# Revit family: DC_Holyoake_MEQ_FSD-200_12
name_source: partatom
category: Air Terminals
revit_build: Autodesk Revit MEP 2013 (Build: 20120221_2030(x64)
units: mm (PartAtom-declared; Revit-internal decimal feet)

## types (1)
- FSD 200
    Connector Rad = 65 mm  [stored 0.213255 ft]
    Description = Floor Swirl Diffusers shall be Holyoake Model FSD-200 Floor Swirl Diffusers. The diffusers shall be constructed entirely of high impact polycarbonate which complies with UL Standard 94-5V for flammability. The core design shall produce a high velocity helical swirl discharge air pattern. The diffusers shall incorporate a removable dust/dirt collection basket. An air flow regulator damper, adjustable without removing the diffuser core, shall be provided with visual open/closed indication and include an adjustable minimum volume stop. Finish on visible surfaces shall be Grey or Black (selected Finishes available).
    Finish = Holyoake Black
    Holyoake Product Range = Holyoake FSD Floor Swirl Diffuser
    Manufacturer = Holyoake
    Material Body = Holyoake Grey
    Material Face = Holyoake Grey
    Max Flow = 70.0 L/s
    Min Flow = 10.0 L/s
    Model = FSD - 200
    Noise Level NC Max = 20 NC
    Noise Level NC Min = 3 NC
    Static Pressure Max = 31.0 Pa
    Static Pressure Min = 3.0 Pa
    Type Comments = Floor Swirl Diffuser
    URL = http://www.holyoake.com

note: [stored X ft] marks values corroborated as IEEE doubles in the binary element streams (Revit-internal decimal feet)

## geometry (parser evidence)
native form markers: Blend x10, Sweep x1
no freeform markers — native parametric forms only
